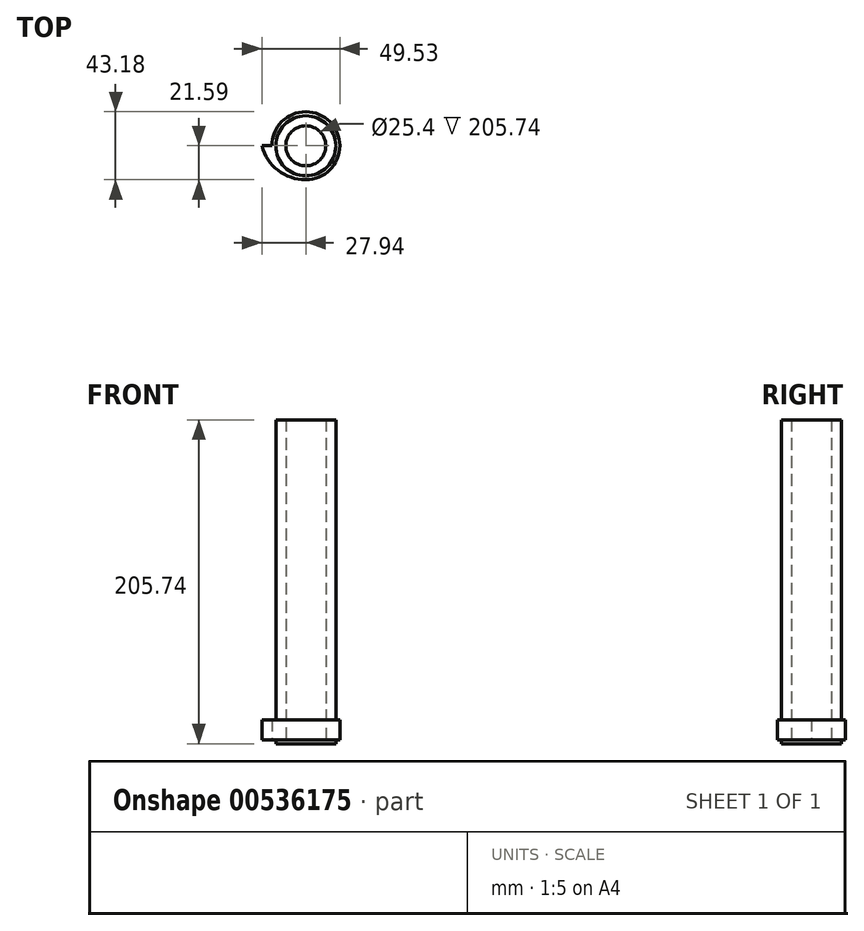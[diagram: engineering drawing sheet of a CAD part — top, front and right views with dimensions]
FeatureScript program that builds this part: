
annotation { "Feature Type Name" : "Feature", "Feature Type Description" : "" }
export const myFeature = defineFeature(function(context is Context, id is Id, definition is map)
    precondition{}
    {
        {
            var Q0;
            Q0=qCreatedBy(makeId("Top.planeOp"),FACE);
            var sketch = newSketch(context, id + "F0", { "sketchPlane" : qUnion([Q0])});
            skCircle(sketch, "E0", {"center": v(0, 0) * mm, "radius": 19.05 * mm});
            skSolve(sketch);
        }
        {
            var Q0;
            Q0 = qSketchRegion(id + "F0", true);
            extrude(context, id + "F1", {"entities" : qUnion([Q0]), "depth" : 205.74 * mm, "offsetDistance" : 25.4 * mm});
        }
        {
            var Q0;
            Q0=makeQuery(id+"F1.opExtrude","CAP_FACE",FACE,{"disambiguationData":[OSD([sQuery(id+"F0.wireOp",EDGE,"E0")])],"isStart":true});
            cPlane(context, id + "F2", {"entities" : qUnion([Q0]), "cplaneType" : CPlaneType.OFFSET, "offset" : 2.54 * mm, "oppositeDirection" : true, "width" : 152.4 * mm, "height" : 152.4 * mm});
        }
        {
            var Q0;
            Q0=qCreatedBy(id+"F2.planeOp",FACE);
            cPlane(context, id + "F3", {"entities" : qUnion([Q0]), "cplaneType" : CPlaneType.OFFSET, "offset" : 25.4 * mm, "oppositeDirection" : true, "width" : 152.4 * mm, "height" : 152.4 * mm});
        }
        {
            var Q0;
            Q0=qCreatedBy(id+"F3.planeOp",FACE);
            cPlane(context, id + "F4", {"entities" : qUnion([Q0]), "cplaneType" : CPlaneType.OFFSET, "offset" : 25.4 * mm, "oppositeDirection" : true, "width" : 152.4 * mm, "height" : 152.4 * mm});
        }
        {
            var Q0;
            Q0=qCreatedBy(id+"F4.planeOp",FACE);
            cPlane(context, id + "F5", {"entities" : qUnion([Q0]), "cplaneType" : CPlaneType.OFFSET, "offset" : 25.4 * mm, "oppositeDirection" : true, "width" : 152.4 * mm, "height" : 152.4 * mm});
        }
        {
            var Q0;
            Q0=qCreatedBy(id+"F5.planeOp",FACE);
            cPlane(context, id + "F6", {"entities" : qUnion([Q0]), "cplaneType" : CPlaneType.OFFSET, "offset" : 25.4 * mm, "oppositeDirection" : true, "width" : 152.4 * mm, "height" : 152.4 * mm});
        }
        {
            var Q0;
            Q0=qCreatedBy(id+"F6.planeOp",FACE);
            cPlane(context, id + "F7", {"entities" : qUnion([Q0]), "cplaneType" : CPlaneType.OFFSET, "offset" : 25.4 * mm, "oppositeDirection" : true, "width" : 152.4 * mm, "height" : 152.4 * mm});
        }
        {
            var Q0;
            Q0=qCreatedBy(id+"F7.planeOp",FACE);
            cPlane(context, id + "F8", {"entities" : qUnion([Q0]), "cplaneType" : CPlaneType.OFFSET, "offset" : 25.4 * mm, "oppositeDirection" : true, "width" : 152.4 * mm, "height" : 152.4 * mm});
        }
        {
            var Q0;
            Q0=qCreatedBy(id+"F2.planeOp",FACE);
            var sketch = newSketch(context, id + "F9", { "sketchPlane" : qUnion([Q0])});
            skCircle(sketch, "E1.0", {"center": v(0, 0) * mm, "radius": 19.05 * mm});
            skCircle(sketch, "E2", {"center": v(0, 0) * mm, "radius": 21.59 * mm});
            skLineSegment(sketch, "E3", {"start": v(-21.59, 0) * mm, "end": v(-27.94, 0) * mm});
            skPoint(sketch, "E4", {"position": v(0, 21.59) * mm});
            skArc(sketch, "E5", {"start": v(0, 21.6) * mm, "mid": v(-17.65, 15.56) * mm, "end": v(-27.94, 0) * mm});
            skSolve(sketch);
        }
        {
            var Q0;
            Q0 = qSketchRegion(id + "F9", true);
            extrude(context, id + "F10", {"entities" : qUnion([Q0]), "operationType" : NewBodyOperationType.ADD, "oppositeDirection" : true, "depth" : 12.7 * mm, "offsetDistance" : 25.4 * mm});
        }
        {
            var Q0;
            Q0=makeQuery(id+"F1.opExtrude","CAP_FACE",FACE,{"disambiguationData":[OSD([sQuery(id+"F0.wireOp",EDGE,"E0")])],"isStart":true});
            var sketch = newSketch(context, id + "F11", { "sketchPlane" : qUnion([Q0])});
            skCircle(sketch, "E6", {"center": v(0, 0) * mm, "radius": 12.7 * mm});
            skSolve(sketch);
        }
        {
            var Q0;
            Q0 = qSketchRegion(id + "F11", true);
            extrude(context, id + "F12", {"entities" : qUnion([Q0]), "operationType" : NewBodyOperationType.REMOVE, "oppositeDirection" : true, "depth" : 254 * mm, "offsetDistance" : 25.4 * mm});
        }
    });
